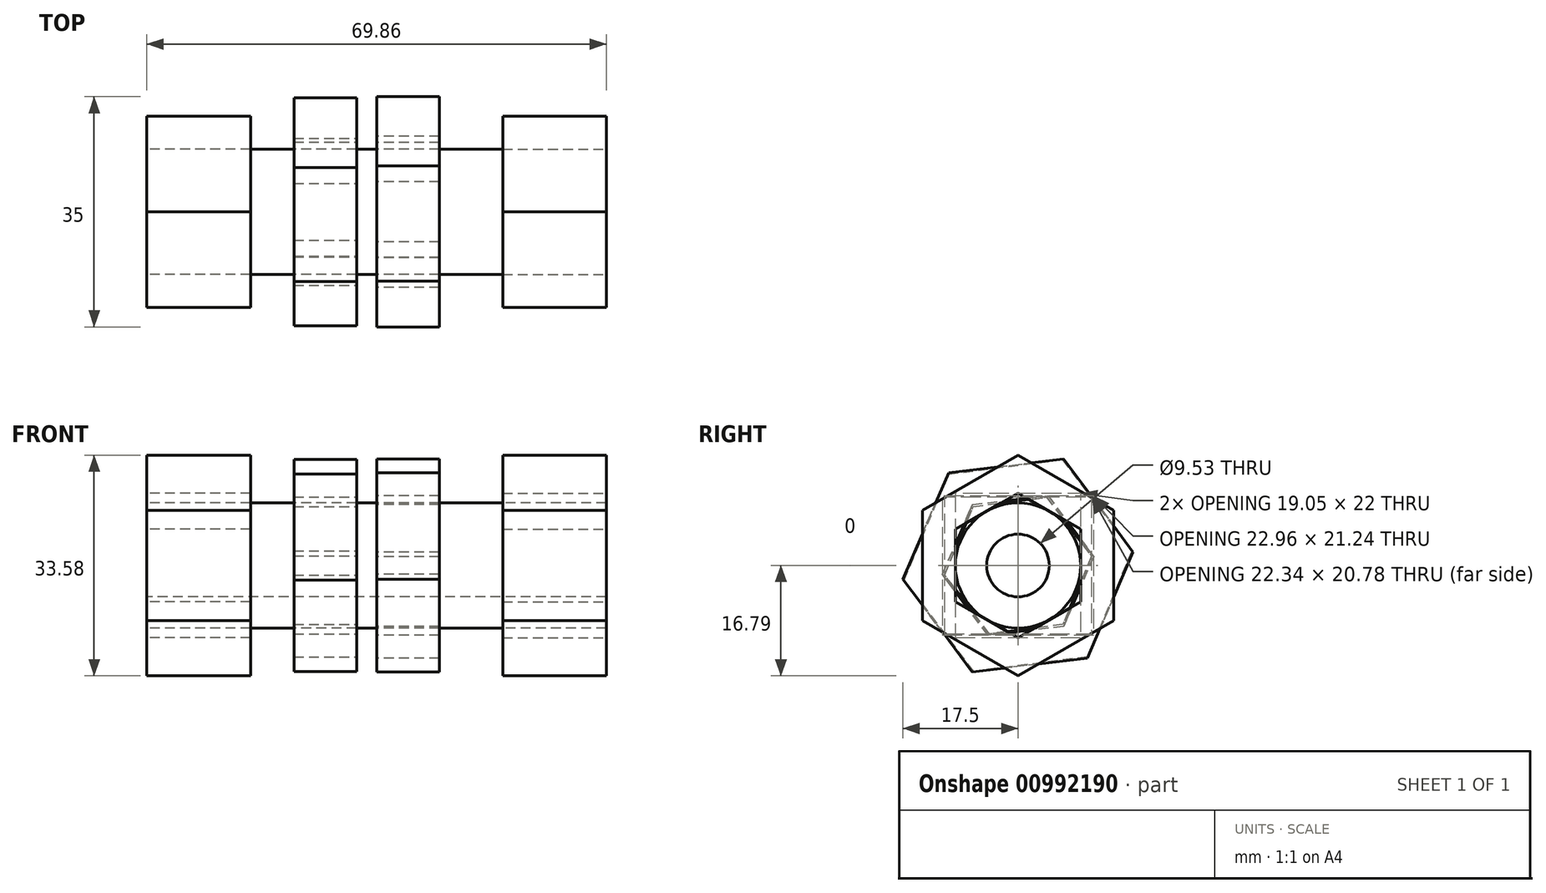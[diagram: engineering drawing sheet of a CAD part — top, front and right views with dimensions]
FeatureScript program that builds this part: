
annotation { "Feature Type Name" : "Feature", "Feature Type Description" : "" }
export const myFeature = defineFeature(function(context is Context, id is Id, definition is map)
    precondition{}
    {
        {
            var Q0;
            Q0=qCreatedBy(makeId("Right.planeOp"),FACE);
            var sketch = newSketch(context, id + "F0", { "sketchPlane" : qUnion([Q0])});
            skCircle(sketch, "E0", {"center": v(0, 0) * mm, "radius": 9.53 * mm});
            skCircle(sketch, "E1", {"center": v(0, 0) * mm, "radius": 4.76 * mm});
            skSolve(sketch);
        }
        {
            var Q0;
            Q0 = qSketchRegion(id + "F0", true);
            extrude(context, id + "F1", {"entities" : qUnion([Q0]), "endBound" : BoundingType.SYMMETRIC, "depth" : 69.85 * mm, "offsetDistance" : 25.4 * mm});
        }
        {
            var Q0;
            Q0=qCreatedBy(makeId("Right.planeOp"),FACE);
            var sketch = newSketch(context, id + "F2", { "sketchPlane" : qUnion([Q0])});
            skCircle(sketch, "E2.cCircle", {"center": v(0, 0) * mm, "radius": 10.01 * mm, "construction": true});
            skLineSegment(sketch, "E2.0", {"start": v(11.48, 1.35) * mm, "end": v(6.91, -9.27) * mm});
            skLineSegment(sketch, "E2.1", {"start": v(6.91, -9.27) * mm, "end": v(-4.57, -10.62) * mm});
            skLineSegment(sketch, "E2.2", {"start": v(-4.57, -10.62) * mm, "end": v(-11.48, -1.35) * mm});
            skLineSegment(sketch, "E2.3", {"start": v(-11.48, -1.35) * mm, "end": v(-6.91, 9.27) * mm});
            skLineSegment(sketch, "E2.4", {"start": v(-6.91, 9.27) * mm, "end": v(4.57, 10.62) * mm});
            skLineSegment(sketch, "E2.5", {"start": v(4.57, 10.62) * mm, "end": v(11.48, 1.35) * mm});
            skPoint(sketch, "E2.0.midPoint", {"position": v(9.2, -3.96) * mm});
            skCircle(sketch, "E3.cCircle", {"center": v(0, 0) * mm, "radius": 15.26 * mm, "construction": true});
            skLineSegment(sketch, "E3.0", {"start": v(17.5, 2.06) * mm, "end": v(10.54, -14.12) * mm});
            skLineSegment(sketch, "E3.1", {"start": v(10.54, -14.12) * mm, "end": v(-6.96, -16.19) * mm});
            skLineSegment(sketch, "E3.2", {"start": v(-6.96, -16.19) * mm, "end": v(-17.5, -2.06) * mm});
            skLineSegment(sketch, "E3.3", {"start": v(-17.5, -2.06) * mm, "end": v(-10.54, 14.12) * mm});
            skLineSegment(sketch, "E3.4", {"start": v(-10.54, 14.12) * mm, "end": v(6.96, 16.19) * mm});
            skLineSegment(sketch, "E3.5", {"start": v(6.96, 16.19) * mm, "end": v(17.5, 2.06) * mm});
            skPoint(sketch, "E3.0.midPoint", {"position": v(14.02, -6.03) * mm});
            skSolve(sketch);
        }
        {
            var Q0;
            Q0 = qSketchRegion(id + "F2", true);
            extrude(context, id + "F3", {"entities" : qUnion([Q0]), "depth" : 9.52 * mm, "offsetDistance" : 25.4 * mm});
        }
        {
            var Q0;
            Q0=qCreatedBy(makeId("Right.planeOp"),FACE);
            cPlane(context, id + "F4", {"entities" : qUnion([Q0]), "cplaneType" : CPlaneType.OFFSET, "offset" : 3.05 * mm, "oppositeDirection" : true, "width" : 152.4 * mm, "height" : 152.4 * mm});
        }
        {
            var Q0;
            Q0=qCreatedBy(id+"F4.planeOp",FACE);
            var sketch = newSketch(context, id + "F5", { "sketchPlane" : qUnion([Q0])});
            skCircle(sketch, "E4.cCircle", {"center": v(0, 0) * mm, "radius": 9.75 * mm, "construction": true});
            skLineSegment(sketch, "E4.0", {"start": v(-11.17, -1.44) * mm, "end": v(-6.83, 8.95) * mm});
            skLineSegment(sketch, "E4.1", {"start": v(-6.83, 8.95) * mm, "end": v(4.34, 10.4) * mm});
            skLineSegment(sketch, "E4.2", {"start": v(4.34, 10.4) * mm, "end": v(11.17, 1.44) * mm});
            skLineSegment(sketch, "E4.3", {"start": v(11.17, 1.44) * mm, "end": v(6.83, -8.95) * mm});
            skLineSegment(sketch, "E4.4", {"start": v(6.83, -8.95) * mm, "end": v(-4.34, -10.4) * mm});
            skLineSegment(sketch, "E4.5", {"start": v(-4.34, -10.4) * mm, "end": v(-11.17, -1.44) * mm});
            skPoint(sketch, "E4.0.midPoint", {"position": v(-9, 3.76) * mm});
            skCircle(sketch, "E5.cCircle", {"center": v(0, 0) * mm, "radius": 15.12 * mm, "construction": true});
            skLineSegment(sketch, "E5.0", {"start": v(-17.32, -2.23) * mm, "end": v(-10.6, 13.89) * mm});
            skLineSegment(sketch, "E5.1", {"start": v(-10.6, 13.89) * mm, "end": v(6.73, 16.12) * mm});
            skLineSegment(sketch, "E5.2", {"start": v(6.73, 16.12) * mm, "end": v(17.32, 2.23) * mm});
            skLineSegment(sketch, "E5.3", {"start": v(17.32, 2.23) * mm, "end": v(10.6, -13.89) * mm});
            skLineSegment(sketch, "E5.4", {"start": v(10.6, -13.89) * mm, "end": v(-6.73, -16.12) * mm});
            skLineSegment(sketch, "E5.5", {"start": v(-6.73, -16.12) * mm, "end": v(-17.32, -2.23) * mm});
            skPoint(sketch, "E5.0.midPoint", {"position": v(-13.96, 5.83) * mm});
            skSolve(sketch);
        }
        {
            var Q0;
            Q0 = qSketchRegion(id + "F5", true);
            extrude(context, id + "F6", {"entities" : qUnion([Q0]), "oppositeDirection" : true, "depth" : 9.52 * mm, "offsetDistance" : 25.4 * mm});
        }
        {
            var Q0;
            Q0=makeQuery(id+"F1.opExtrude","CAP_FACE",FACE,{"disambiguationData":[OSD([sQuery(id+"F0.wireOp",EDGE,"E0"),sQuery(id+"F0.wireOp",EDGE,"E1")])],"isStart":true});
            var sketch = newSketch(context, id + "F7", { "sketchPlane" : qUnion([Q0])});
            skCircle(sketch, "E6.cCircle", {"center": v(0, 0) * mm, "radius": 9.53 * mm, "construction": true});
            skLineSegment(sketch, "E6.0", {"start": v(9.53, 5.5) * mm, "end": v(9.53, -5.5) * mm});
            skLineSegment(sketch, "E6.1", {"start": v(9.53, -5.5) * mm, "end": v(0, -11) * mm});
            skLineSegment(sketch, "E6.2", {"start": v(0, -11) * mm, "end": v(-9.52, -5.5) * mm});
            skLineSegment(sketch, "E6.3", {"start": v(-9.53, -5.5) * mm, "end": v(-9.53, 5.5) * mm});
            skLineSegment(sketch, "E6.4", {"start": v(-9.53, 5.5) * mm, "end": v(0, 11) * mm});
            skLineSegment(sketch, "E6.5", {"start": v(0, 11) * mm, "end": v(9.53, 5.5) * mm});
            skPoint(sketch, "E6.0.midPoint", {"position": v(9.53, 0) * mm});
            skCircle(sketch, "E7.cCircle", {"center": v(0, 0) * mm, "radius": 14.54 * mm, "construction": true});
            skLineSegment(sketch, "E7.0", {"start": v(14.54, 8.4) * mm, "end": v(14.54, -8.4) * mm});
            skLineSegment(sketch, "E7.1", {"start": v(14.54, -8.4) * mm, "end": v(0, -16.79) * mm});
            skLineSegment(sketch, "E7.2", {"start": v(0, -16.79) * mm, "end": v(-14.54, -8.4) * mm});
            skLineSegment(sketch, "E7.3", {"start": v(-14.54, -8.4) * mm, "end": v(-14.54, 8.4) * mm});
            skLineSegment(sketch, "E7.4", {"start": v(-14.54, 8.4) * mm, "end": v(0, 16.79) * mm});
            skLineSegment(sketch, "E7.5", {"start": v(0, 16.79) * mm, "end": v(14.54, 8.4) * mm});
            skPoint(sketch, "E7.0.midPoint", {"position": v(14.54, 0) * mm});
            skSolve(sketch);
        }
        {
            var Q0;
            Q0 = qSketchRegion(id + "F7", true);
            extrude(context, id + "F8", {"entities" : qUnion([Q0]), "oppositeDirection" : true, "depth" : 15.75 * mm, "offsetDistance" : 25.4 * mm});
        }
        {
            var Q0;
            Q0=makeQuery(id+"F1.opExtrude","CAP_FACE",FACE,{"disambiguationData":[OSD([sQuery(id+"F0.wireOp",EDGE,"E0"),sQuery(id+"F0.wireOp",EDGE,"E1")])],"isStart":false});
            var sketch = newSketch(context, id + "F9", { "sketchPlane" : qUnion([Q0])});
            skCircle(sketch, "E8.cCircle", {"center": v(0, 0) * mm, "radius": 9.53 * mm, "construction": true});
            skLineSegment(sketch, "E8.0", {"start": v(9.53, 5.5) * mm, "end": v(9.53, -5.5) * mm});
            skLineSegment(sketch, "E8.1", {"start": v(9.53, -5.5) * mm, "end": v(0, -11) * mm});
            skLineSegment(sketch, "E8.2", {"start": v(0, -11) * mm, "end": v(-9.52, -5.5) * mm});
            skLineSegment(sketch, "E8.3", {"start": v(-9.53, -5.5) * mm, "end": v(-9.53, 5.5) * mm});
            skLineSegment(sketch, "E8.4", {"start": v(-9.53, 5.5) * mm, "end": v(0, 11) * mm});
            skLineSegment(sketch, "E8.5", {"start": v(0, 11) * mm, "end": v(9.53, 5.5) * mm});
            skPoint(sketch, "E8.0.midPoint", {"position": v(9.53, 0) * mm});
            skCircle(sketch, "E9.cCircle", {"center": v(0, 0) * mm, "radius": 14.54 * mm, "construction": true});
            skLineSegment(sketch, "E9.0", {"start": v(14.54, 8.4) * mm, "end": v(14.54, -8.4) * mm});
            skLineSegment(sketch, "E9.1", {"start": v(14.54, -8.4) * mm, "end": v(0, -16.79) * mm});
            skLineSegment(sketch, "E9.2", {"start": v(0, -16.79) * mm, "end": v(-14.54, -8.4) * mm});
            skLineSegment(sketch, "E9.3", {"start": v(-14.54, -8.4) * mm, "end": v(-14.54, 8.4) * mm});
            skLineSegment(sketch, "E9.4", {"start": v(-14.54, 8.4) * mm, "end": v(0, 16.79) * mm});
            skLineSegment(sketch, "E9.5", {"start": v(0, 16.79) * mm, "end": v(14.54, 8.4) * mm});
            skPoint(sketch, "E9.0.midPoint", {"position": v(14.54, 0) * mm});
            skSolve(sketch);
        }
        {
            var Q0;
            Q0 = qSketchRegion(id + "F9", true);
            extrude(context, id + "F10", {"entities" : qUnion([Q0]), "oppositeDirection" : true, "depth" : 15.75 * mm, "offsetDistance" : 25.4 * mm});
        }
    });
